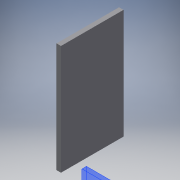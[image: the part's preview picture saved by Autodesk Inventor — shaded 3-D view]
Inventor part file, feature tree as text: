
AUTODESK INVENTOR PART (.ipt)
format: ipt  version: 2017 (Build 210142000, 142)  size: 87,552 bytes
history: native  units: mm
features: extrude x1, sketch x1
ambient origin geometry x8: Origin, YZ Plane, XZ Plane, XY Plane, X Axis, Y Axis, Z Axis, Center Point
bodies: Solid1 (feature_tree)
feature tree (2):
  extrude  "Extrusion1"  [1 undecoded]
  sketch  "Sketch1"  dims[d0=361.75mm d1=0.0mm]
note: 1 required parameter value undecoded (feature->parameter linkage not recoverable at this tier; creation-order binding heuristic only, values carry confidence <= 0.55)
